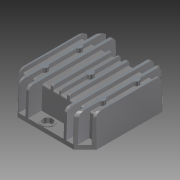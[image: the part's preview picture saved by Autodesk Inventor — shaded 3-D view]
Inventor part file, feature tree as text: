
AUTODESK INVENTOR PART (.ipt)
format: ipt  version: 2014 (Build 180170000, 170)  size: 353,792 bytes
history: native  units: in
note: dims shown in document units (in); Inventor stores cm internally (conversion verified against a paired STEP export)
features: extrude x8, sketch x7, plane x3, fillet x3, mirror x2, projected_geometry x1
ambient origin geometry x8: Origin, YZ Plane, XZ Plane, XY Plane, X Axis, Y Axis, Z Axis, Center Point
bodies: Solid1 (feature_tree)
feature tree (24):
  sketch  "Sketch1"  dims[d0=0.906in d1=-0.0137in d4=0.25in d5=0.25in]
  extrude  "Extrusion1"  Depth=0.906in
  extrude  "Extrusion3"  Depth=0.047in
  plane  "Work Plane1"
  mirror  "Mirror1"
  plane  "Work Plane2"
  extrude  "Extrusion4"  Depth=0.079in
  extrude  "Extrusion5"  Depth=0.079in
  extrude  "Extrusion6"  Depth=0.2403in
  extrude  "Extrusion7"  TaperAngle=0.0deg  [1 undecoded]
  fillet  "Fillet1"  Radius=0.787in
  fillet  "Fillet2"  Radius=0.787in
  fillet  "Fillet3"  Radius=0.787in
  extrude  "Extrusion8"  Depth=0.125in
  plane  "Work Plane3"
  mirror  "Mirror2"
  extrude  "Extrusion9"  Depth=0.05in
  sketch  "Sketch4"  dims[d6=0.25in d7=0.047in]
  sketch  "Sketch5"  dims[d8=0.202in d9=0.079in]
  sketch  "Sketch7"  dims[d10=0.202in d11=0.079in]
  sketch  "Sketch8"  dims[d12=0.787in d13=0.0in d14=0.2403in]
  sketch  "Sketch9"  dims[d16=0.182in d17=0.0in d18=0.787in d19=0.0in d20=0.787in d21=0.0in d22=0.787in d23=0.0in]
  projected_geometry  "Projected Loop1"
  sketch  "Sketch10"  dims[d24=0.787in d25=0.0in d26=0.125in d27=0.05in d28=0.05in d29=0.2in d32=1.0in d33=0.787in d34=0.0in d35=0.375in d37=0.02in d38=-0.0137in]
note: 1 required parameter value undecoded (feature->parameter linkage not recoverable at this tier; creation-order binding heuristic only, values carry confidence <= 0.55)
